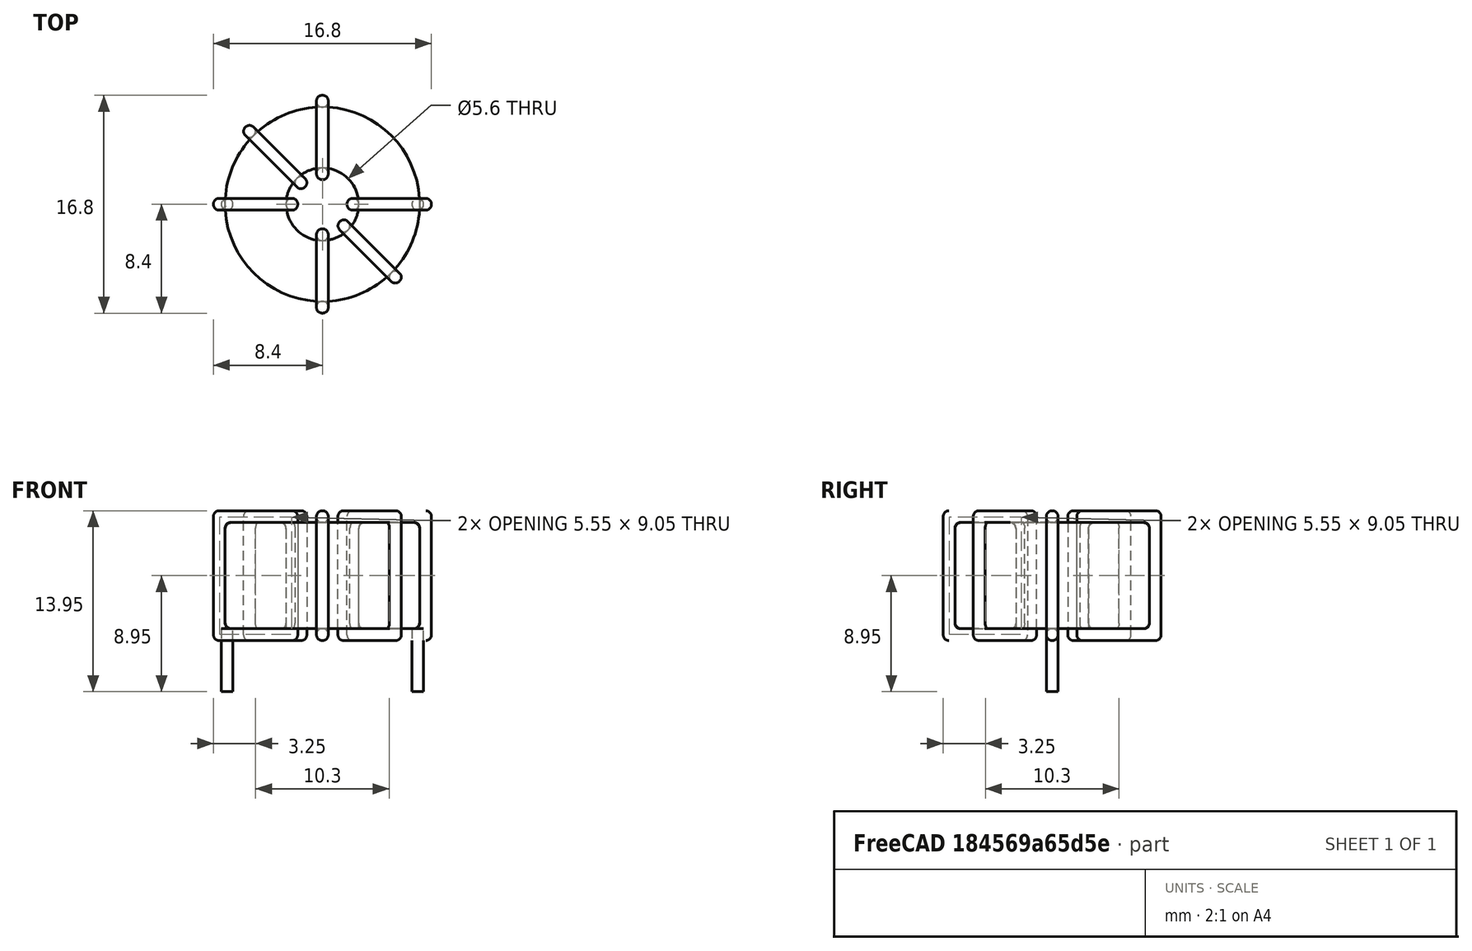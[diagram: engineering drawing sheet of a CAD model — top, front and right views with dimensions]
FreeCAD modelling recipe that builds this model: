
FCSTD DOCUMENT  (FreeCAD 0.16R6703 (Git))
Label: L_Toroid_Horizontal_D16.8mm_P14.70mm_Vishay_TJ3
License: All rights reserved
LicenseURL: http://en.wikipedia.org/wiki/All_rights_reserved
objects: Sketcher::SketchObject×6, PartDesign::Pad×6, PartDesign::Fillet×5, Spreadsheet::Sheet×1
note: 23 computed .brp shape members not serialized (recipe doc carries the construction recipe); baked Part::Feature solids carry a one-line shape summary decoded from their .brp

FEATURE [Spreadsheet::Sheet] Spreadsheet  label="dimensions"
  cells = A1=Wx; B1(Wx)=16.8; C1(WW)=5.600000000000001; D1=16.8; A2=Wy; B2(Wy)=16.8; D2=16.8; A3=RM; B3(RMx)=14.7; C3(RMy)=0; A4=d_wire; B4(d_wire)=0.8999999999999999; A5=H; B5(H)=8.199999999999999; A6=offsetx; B6(offsetx)=1.050000000000001
FEATURE [Sketcher::SketchObject] Sketch
  Placement = pos=(0,0,1.4) rot=(0,0,1;0rad)
  expr: Placement.Base.z = 0.5 + Spreadsheet.d_wire
  expr: Constraints[0] = Spreadsheet.Wx / 2 - Spreadsheet.d_wire
  expr: Constraints[4] = Spreadsheet.WW / 2
  expr: Constraints[2] = Spreadsheet.RMy / 2
  expr: Constraints[1] = Spreadsheet.RMx / 2
  sketch-geometry (2):
    g0: Circle CenterX=7.35 CenterY=0 CenterZ=0 NormalX=0 NormalY=0 NormalZ=1 Radius=7.5
    g1: Circle CenterX=7.35 CenterY=0 CenterZ=0 NormalX=0 NormalY=0 NormalZ=1 Radius=2.8
  constraints (5):
    c: Radius(g0) = 7.5
    c: DistanceX(g-1,g0) = 7.35
    c: DistanceY(g-1,g0) = 0
    c: Coincident(g1,g0)
    c: Radius(g1) = 2.8
FEATURE [PartDesign::Pad] Pad
  Length = 8.2
  Length2 = 100
  Placement = pos=(0,0,1.4) rot=(0,0,1;0rad)
  Sketch = -> Sketch
  Type = 0
  expr: Length = Spreadsheet.H
FEATURE [Sketcher::SketchObject] Sketch001
  Placement = pos=(0,0,0.95) rot=(0,0,1;0rad)
  expr: Placement.Base.z = 0.5 + Spreadsheet.d_wire * 0.5
  expr: Constraints[4] = Spreadsheet.RMx
  expr: Constraints[2] = Spreadsheet.RMy
  expr: Constraints[1] = Spreadsheet.d_wire / 2
  sketch-geometry (2):
    g0: Circle CenterX=0 CenterY=0 CenterZ=0 NormalX=0 NormalY=0 NormalZ=1 Radius=0.45
    g1: Circle CenterX=14.7 CenterY=0 CenterZ=0 NormalX=0 NormalY=0 NormalZ=1 Radius=0.45
  constraints (5):
    c: Equal(g0,g1)
    c: Radius(g0) = 0.45
    c: DistanceY(g-1,g1) = 0
    c: Coincident(g0,g-1)
    c: DistanceX(g-1,g1) = 14.7
FEATURE [PartDesign::Pad] Pad001
  Length = 0.45
  Length2 = 4.4
  Placement = pos=(0,0,0.95) rot=(0,0,1;0rad)
  Reversed = true
  Sketch = -> Sketch001
  Type = 4
  expr: Length2 = 3.5 + Spreadsheet.d_wire
  expr: Length = Spreadsheet.d_wire / 2
FEATURE [PartDesign::Fillet] Fillet
  Base = -> Pad [Edge6,Edge3,Edge2]
  Placement = pos=(0,0,1.4) rot=(0,0,1;0rad)
  Radius = 0.5
FEATURE [Sketcher::SketchObject] Sketch003
  Placement = pos=(7.35,0,0) rot=(1,0,0;1.5708rad)
  expr: Placement.Base.x = Spreadsheet.RMx / 2
  expr: Constraints[49] = Spreadsheet.Wx - Spreadsheet.d_wire * 2
  expr: Constraints[44] = Spreadsheet.d_wire
  expr: Constraints[23] = Spreadsheet.H
  expr: Constraints[22] = Spreadsheet.Wx / 2 - Spreadsheet.d_wire
  expr: Placement.Base.y = Spreadsheet.RMy / 2
  expr: Constraints[21] = (Spreadsheet.Wx - Spreadsheet.WW) / 2 - Spreadsheet.d_wire
  expr: Constraints[19] = Spreadsheet.d_wire
  expr: Constraints[17] = Spreadsheet.d_wire
  expr: Constraints[18] = Spreadsheet.d_wire
  expr: Constraints[16] = Spreadsheet.d_wire
  sketch-geometry (16):
    g0: LineSegment StartX=-1.9 StartY=0.5 StartZ=0 EndX=-8.4 EndY=0.5 EndZ=0
    g1: LineSegment StartX=-8.4 StartY=0.5 StartZ=0 EndX=-8.4 EndY=10.5 EndZ=0
    g2: LineSegment StartX=-8.4 StartY=10.5 StartZ=0 EndX=-1.9 EndY=10.5 EndZ=0
    g3: LineSegment StartX=-1.9 StartY=10.5 StartZ=0 EndX=-1.9 EndY=0.5 EndZ=0
    g4: LineSegment StartX=-7.5 StartY=9.6 StartZ=0 EndX=-2.8 EndY=9.6 EndZ=0
    g5: LineSegment StartX=-2.8 StartY=9.6 StartZ=0 EndX=-2.8 EndY=1.4 EndZ=0
    g6: LineSegment StartX=-2.8 StartY=1.4 StartZ=0 EndX=-7.5 EndY=1.4 EndZ=0
    g7: LineSegment StartX=-7.5 StartY=1.4 StartZ=0 EndX=-7.5 EndY=9.6 EndZ=0
    g8: LineSegment StartX=1.9 StartY=10.5 StartZ=0 EndX=8.4 EndY=10.5 EndZ=0
    g9: LineSegment StartX=8.4 StartY=10.5 StartZ=0 EndX=8.4 EndY=0.5 EndZ=0
    g10: LineSegment StartX=8.4 StartY=0.5 StartZ=0 EndX=1.9 EndY=0.5 EndZ=0
    g11: LineSegment StartX=1.9 StartY=0.5 StartZ=0 EndX=1.9 EndY=10.5 EndZ=0
    g12: LineSegment StartX=2.8 StartY=9.6 StartZ=0 EndX=7.5 EndY=9.6 EndZ=0
    g13: LineSegment StartX=7.5 StartY=9.6 StartZ=0 EndX=7.5 EndY=1.4 EndZ=0
    g14: LineSegment StartX=7.5 StartY=1.4 StartZ=0 EndX=2.8 EndY=1.4 EndZ=0
    g15: LineSegment StartX=2.8 StartY=1.4 StartZ=0 EndX=2.8 EndY=9.6 EndZ=0
  constraints (50):
    c: Horizontal(g0)
    c: Coincident(g1,g0)
    c: Vertical(g1)
    c: Coincident(g2,g1)
    c: Horizontal(g2)
    c: Coincident(g3,g2)
    c: Coincident(g3,g0)
    c: Vertical(g3)
    c: Coincident(g4,g5)
    c: Coincident(g5,g6)
    c: Coincident(g6,g7)
    c: Coincident(g7,g4)
    c: Horizontal(g4)
    c: Horizontal(g6)
    c: Vertical(g5)
    c: Vertical(g7)
    c: DistanceX(g1,g4) = 0.9
    c: DistanceY(g4,g1) = 0.9
    c: DistanceX(g5,g0) = 0.9
    c: DistanceY(g0,g5) = 0.9
    c: DistanceY(g-1,g0) = 0.5
    c: DistanceX(g6,g6) = 4.7
    c: DistanceX(g6,g-1) = 7.5
    c: DistanceY(g7,g7) = 8.2
    c: Coincident(g8,g9)
    c: Coincident(g9,g10)
    c: Coincident(g10,g11)
    c: Coincident(g11,g8)
    c: Horizontal(g8)
    c: Horizontal(g10)
    c: Vertical(g9)
    c: Vertical(g11)
    c: Coincident(g12,g13)
    c: Coincident(g13,g14)
    c: Coincident(g14,g15)
    c: Coincident(g15,g12)
    c: Horizontal(g12)
    c: Horizontal(g14)
    c: Vertical(g13)
    c: Vertical(g15)
    c: DistanceY(g8,g2) = 0
    c: DistanceY(g10,g0) = 0
    c: DistanceY(g14,g5) = 0
    c: DistanceY(g12,g4) = 0
    c: DistanceX(g8,g12) = 0.9
    c: Equal(g8,g2)
    c: Equal(g12,g4)
    c: Equal(g9,g1)
    c: Equal(g13,g7)
    c: DistanceX(g4,g12) = 15
FEATURE [PartDesign::Pad] Pad002
  Length = 0.9
  Length2 = 100
  Midplane = true
  Placement = pos=(7.35,0,0) rot=(1,0,0;1.5708rad)
  Sketch = -> Sketch003
  Type = 0
  expr: Length = Spreadsheet.d_wire
FEATURE [PartDesign::Fillet] Fillet001
  Base = -> Pad002 [Edge38,Edge41,Edge42,Edge43,Edge29,Edge32,Edge33,Edge34,Edge25,Edge35,Edge36,Edge13,Edge14,Edge15,Edge16,Edge17,Edge18,Edge19,Edge1,Edge2,Edge3,Edge4,Edge5,Edge6,Edge7,Edge37,Edge39,Edge40,Edge20,Edge23,Edge24,Edge21,Edge22,Edge8,Edge9,Edge10,Edge11,Edge12,Edge26,Edge27,+8 more]
  Placement = pos=(7.35,0,0) rot=(1,0,0;1.5708rad)
  Radius = 0.423
  expr: Radius = Spreadsheet.d_wire * 0.47
FEATURE [Sketcher::SketchObject] Sketch004
  Placement = pos=(7.35,0,0) rot=(0.862856,0.357407,0.357407;1.71777rad)
  expr: Placement.Base.x = Spreadsheet.RMx / 2
  expr: Constraints[49] = Spreadsheet.Wx - 2 * Spreadsheet.d_wire
  expr: Constraints[44] = Spreadsheet.d_wire
  expr: Constraints[23] = Spreadsheet.H
  expr: Constraints[22] = Spreadsheet.Wx / 2 - Spreadsheet.d_wire
  expr: Placement.Base.y = Spreadsheet.RMy / 2
  expr: Constraints[21] = (Spreadsheet.Wx - Spreadsheet.WW) / 2 - Spreadsheet.d_wire
  expr: Constraints[19] = Spreadsheet.d_wire
  expr: Constraints[17] = Spreadsheet.d_wire
  expr: Constraints[18] = Spreadsheet.d_wire
  expr: Constraints[16] = Spreadsheet.d_wire
  sketch-geometry (16):
    g0: LineSegment StartX=-1.9 StartY=0.5 StartZ=0 EndX=-8.4 EndY=0.5 EndZ=0
    g1: LineSegment StartX=-8.4 StartY=0.5 StartZ=0 EndX=-8.4 EndY=10.5 EndZ=0
    g2: LineSegment StartX=-8.4 StartY=10.5 StartZ=0 EndX=-1.9 EndY=10.5 EndZ=0
    g3: LineSegment StartX=-1.9 StartY=10.5 StartZ=0 EndX=-1.9 EndY=0.5 EndZ=0
    g4: LineSegment StartX=-7.5 StartY=9.6 StartZ=0 EndX=-2.8 EndY=9.6 EndZ=0
    g5: LineSegment StartX=-2.8 StartY=9.6 StartZ=0 EndX=-2.8 EndY=1.4 EndZ=0
    g6: LineSegment StartX=-2.8 StartY=1.4 StartZ=0 EndX=-7.5 EndY=1.4 EndZ=0
    g7: LineSegment StartX=-7.5 StartY=1.4 StartZ=0 EndX=-7.5 EndY=9.6 EndZ=0
    g8: LineSegment StartX=1.9 StartY=10.5 StartZ=0 EndX=8.4 EndY=10.5 EndZ=0
    g9: LineSegment StartX=8.4 StartY=10.5 StartZ=0 EndX=8.4 EndY=0.5 EndZ=0
    g10: LineSegment StartX=8.4 StartY=0.5 StartZ=0 EndX=1.9 EndY=0.5 EndZ=0
    g11: LineSegment StartX=1.9 StartY=0.5 StartZ=0 EndX=1.9 EndY=10.5 EndZ=0
    g12: LineSegment StartX=2.8 StartY=9.6 StartZ=0 EndX=7.5 EndY=9.6 EndZ=0
    g13: LineSegment StartX=7.5 StartY=9.6 StartZ=0 EndX=7.5 EndY=1.4 EndZ=0
    g14: LineSegment StartX=7.5 StartY=1.4 StartZ=0 EndX=2.8 EndY=1.4 EndZ=0
    g15: LineSegment StartX=2.8 StartY=1.4 StartZ=0 EndX=2.8 EndY=9.6 EndZ=0
  constraints (50):
    c: Horizontal(g0)
    c: Coincident(g1,g0)
    c: Vertical(g1)
    c: Coincident(g2,g1)
    c: Horizontal(g2)
    c: Coincident(g3,g2)
    c: Coincident(g3,g0)
    c: Vertical(g3)
    c: Coincident(g4,g5)
    c: Coincident(g5,g6)
    c: Coincident(g6,g7)
    c: Coincident(g7,g4)
    c: Horizontal(g4)
    c: Horizontal(g6)
    c: Vertical(g5)
    c: Vertical(g7)
    c: DistanceX(g1,g4) = 0.9
    c: DistanceY(g4,g1) = 0.9
    c: DistanceX(g5,g0) = 0.9
    c: DistanceY(g0,g5) = 0.9
    c: DistanceY(g-1,g0) = 0.5
    c: DistanceX(g6,g6) = 4.7
    c: DistanceX(g6,g-1) = 7.5
    c: DistanceY(g7,g7) = 8.2
    c: Coincident(g8,g9)
    c: Coincident(g9,g10)
    c: Coincident(g10,g11)
    c: Coincident(g11,g8)
    c: Horizontal(g8)
    c: Horizontal(g10)
    c: Vertical(g9)
    c: Vertical(g11)
    c: Coincident(g12,g13)
    c: Coincident(g13,g14)
    c: Coincident(g14,g15)
    c: Coincident(g15,g12)
    c: Horizontal(g12)
    c: Horizontal(g14)
    c: Vertical(g13)
    c: Vertical(g15)
    c: DistanceY(g8,g2) = 0
    c: DistanceY(g10,g0) = 0
    c: DistanceY(g14,g5) = 0
    c: DistanceY(g12,g4) = 0
    c: DistanceX(g8,g12) = 0.9
    c: Equal(g8,g2)
    c: Equal(g12,g4)
    c: Equal(g9,g1)
    c: Equal(g13,g7)
    c: DistanceX(g4,g12) = 15
FEATURE [PartDesign::Pad] Pad003
  Length = 0.9
  Length2 = 100
  Midplane = true
  Placement = pos=(7.35,0,0) rot=(0.862856,0.357407,0.357407;1.71777rad)
  Sketch = -> Sketch004
  Type = 0
  expr: Length = Spreadsheet.d_wire
FEATURE [PartDesign::Fillet] Fillet002
  Base = -> Pad003 [Edge38,Edge41,Edge42,Edge43,Edge29,Edge32,Edge33,Edge34,Edge25,Edge35,Edge36,Edge13,Edge14,Edge15,Edge16,Edge17,Edge18,Edge19,Edge1,Edge2,Edge3,Edge4,Edge5,Edge6,Edge7,Edge37,Edge39,Edge40,Edge20,Edge23,Edge24,Edge21,Edge22,Edge8,Edge9,Edge10,Edge11,Edge12,Edge26,Edge27,+8 more]
  Placement = pos=(7.35,0,0) rot=(0.862856,0.357407,0.357407;1.71777rad)
  Radius = 0.423
  expr: Radius = Spreadsheet.d_wire * 0.47
FEATURE [Sketcher::SketchObject] Sketch005
  Placement = pos=(7.35,0,0) rot=(0.862856,-0.357407,-0.357407;1.71777rad)
  expr: Placement.Base.x = Spreadsheet.RMx / 2
  expr: Constraints[49] = Spreadsheet.Wx - 2 * Spreadsheet.d_wire
  expr: Constraints[44] = Spreadsheet.d_wire
  expr: Constraints[23] = Spreadsheet.H
  expr: Constraints[22] = Spreadsheet.Wx / 2 - Spreadsheet.d_wire
  expr: Placement.Base.y = Spreadsheet.RMy / 2
  expr: Constraints[21] = (Spreadsheet.Wx - Spreadsheet.WW) / 2 - Spreadsheet.d_wire
  expr: Constraints[19] = Spreadsheet.d_wire
  expr: Constraints[17] = Spreadsheet.d_wire
  expr: Constraints[18] = Spreadsheet.d_wire
  expr: Constraints[16] = Spreadsheet.d_wire
  sketch-geometry (16):
    g0: LineSegment StartX=-1.9 StartY=0.5 StartZ=0 EndX=-8.4 EndY=0.5 EndZ=0
    g1: LineSegment StartX=-8.4 StartY=0.5 StartZ=0 EndX=-8.4 EndY=10.5 EndZ=0
    g2: LineSegment StartX=-8.4 StartY=10.5 StartZ=0 EndX=-1.9 EndY=10.5 EndZ=0
    g3: LineSegment StartX=-1.9 StartY=10.5 StartZ=0 EndX=-1.9 EndY=0.5 EndZ=0
    g4: LineSegment StartX=-7.5 StartY=9.6 StartZ=0 EndX=-2.8 EndY=9.6 EndZ=0
    g5: LineSegment StartX=-2.8 StartY=9.6 StartZ=0 EndX=-2.8 EndY=1.4 EndZ=0
    g6: LineSegment StartX=-2.8 StartY=1.4 StartZ=0 EndX=-7.5 EndY=1.4 EndZ=0
    g7: LineSegment StartX=-7.5 StartY=1.4 StartZ=0 EndX=-7.5 EndY=9.6 EndZ=0
    g8: LineSegment StartX=1.9 StartY=10.5 StartZ=0 EndX=8.4 EndY=10.5 EndZ=0
    g9: LineSegment StartX=8.4 StartY=10.5 StartZ=0 EndX=8.4 EndY=0.5 EndZ=0
    g10: LineSegment StartX=8.4 StartY=0.5 StartZ=0 EndX=1.9 EndY=0.5 EndZ=0
    g11: LineSegment StartX=1.9 StartY=0.5 StartZ=0 EndX=1.9 EndY=10.5 EndZ=0
    g12: LineSegment StartX=2.8 StartY=9.6 StartZ=0 EndX=7.5 EndY=9.6 EndZ=0
    g13: LineSegment StartX=7.5 StartY=9.6 StartZ=0 EndX=7.5 EndY=1.4 EndZ=0
    g14: LineSegment StartX=7.5 StartY=1.4 StartZ=0 EndX=2.8 EndY=1.4 EndZ=0
    g15: LineSegment StartX=2.8 StartY=1.4 StartZ=0 EndX=2.8 EndY=9.6 EndZ=0
  constraints (50):
    c: Horizontal(g0)
    c: Coincident(g1,g0)
    c: Vertical(g1)
    c: Coincident(g2,g1)
    c: Horizontal(g2)
    c: Coincident(g3,g2)
    c: Coincident(g3,g0)
    c: Vertical(g3)
    c: Coincident(g4,g5)
    c: Coincident(g5,g6)
    c: Coincident(g6,g7)
    c: Coincident(g7,g4)
    c: Horizontal(g4)
    c: Horizontal(g6)
    c: Vertical(g5)
    c: Vertical(g7)
    c: DistanceX(g1,g4) = 0.9
    c: DistanceY(g4,g1) = 0.9
    c: DistanceX(g5,g0) = 0.9
    c: DistanceY(g0,g5) = 0.9
    c: DistanceY(g-1,g0) = 0.5
    c: DistanceX(g6,g6) = 4.7
    c: DistanceX(g6,g-1) = 7.5
    c: DistanceY(g7,g7) = 8.2
    c: Coincident(g8,g9)
    c: Coincident(g9,g10)
    c: Coincident(g10,g11)
    c: Coincident(g11,g8)
    c: Horizontal(g8)
    c: Horizontal(g10)
    c: Vertical(g9)
    c: Vertical(g11)
    c: Coincident(g12,g13)
    c: Coincident(g13,g14)
    c: Coincident(g14,g15)
    c: Coincident(g15,g12)
    c: Horizontal(g12)
    c: Horizontal(g14)
    c: Vertical(g13)
    c: Vertical(g15)
    c: DistanceY(g8,g2) = 0
    c: DistanceY(g10,g0) = 0
    c: DistanceY(g14,g5) = 0
    c: DistanceY(g12,g4) = 0
    c: DistanceX(g8,g12) = 0.9
    c: Equal(g8,g2)
    c: Equal(g12,g4)
    c: Equal(g9,g1)
    c: Equal(g13,g7)
    c: DistanceX(g4,g12) = 15
FEATURE [PartDesign::Pad] Pad004
  Length = 0.9
  Length2 = 100
  Midplane = true
  Placement = pos=(7.35,0,0) rot=(0.862856,-0.357407,-0.357407;1.71777rad)
  Sketch = -> Sketch005
  Type = 0
  expr: Length = Spreadsheet.d_wire
FEATURE [PartDesign::Fillet] Fillet003
  Base = -> Pad004 [Edge38,Edge41,Edge42,Edge43,Edge29,Edge32,Edge33,Edge34,Edge25,Edge35,Edge36,Edge13,Edge14,Edge15,Edge16,Edge17,Edge18,Edge19,Edge1,Edge2,Edge3,Edge4,Edge5,Edge6,Edge7,Edge37,Edge39,Edge40,Edge20,Edge23,Edge24,Edge21,Edge22,Edge8,Edge9,Edge10,Edge11,Edge12,Edge26,Edge27,+8 more]
  Placement = pos=(7.35,0,0) rot=(0.862856,-0.357407,-0.357407;1.71777rad)
  Radius = 0.423
  expr: Radius = Spreadsheet.d_wire * 0.47
FEATURE [Sketcher::SketchObject] Sketch006
  Placement = pos=(7.35,0,0) rot=(0.57735,0.57735,0.57735;2.0944rad)
  expr: Placement.Base.x = Spreadsheet.RMx / 2
  expr: Constraints[49] = Spreadsheet.Wx - Spreadsheet.d_wire * 2
  expr: Constraints[44] = Spreadsheet.d_wire
  expr: Constraints[23] = Spreadsheet.H
  expr: Constraints[22] = Spreadsheet.Wx / 2 - Spreadsheet.d_wire
  expr: Placement.Base.y = Spreadsheet.RMy / 2
  expr: Constraints[21] = (Spreadsheet.Wx - Spreadsheet.WW) / 2 - Spreadsheet.d_wire
  expr: Constraints[19] = Spreadsheet.d_wire
  expr: Constraints[17] = Spreadsheet.d_wire
  expr: Constraints[18] = Spreadsheet.d_wire
  expr: Constraints[16] = Spreadsheet.d_wire
  sketch-geometry (16):
    g0: LineSegment StartX=-1.9 StartY=0.5 StartZ=0 EndX=-8.4 EndY=0.5 EndZ=0
    g1: LineSegment StartX=-8.4 StartY=0.5 StartZ=0 EndX=-8.4 EndY=10.5 EndZ=0
    g2: LineSegment StartX=-8.4 StartY=10.5 StartZ=0 EndX=-1.9 EndY=10.5 EndZ=0
    g3: LineSegment StartX=-1.9 StartY=10.5 StartZ=0 EndX=-1.9 EndY=0.5 EndZ=0
    g4: LineSegment StartX=-7.5 StartY=9.6 StartZ=0 EndX=-2.8 EndY=9.6 EndZ=0
    g5: LineSegment StartX=-2.8 StartY=9.6 StartZ=0 EndX=-2.8 EndY=1.4 EndZ=0
    g6: LineSegment StartX=-2.8 StartY=1.4 StartZ=0 EndX=-7.5 EndY=1.4 EndZ=0
    g7: LineSegment StartX=-7.5 StartY=1.4 StartZ=0 EndX=-7.5 EndY=9.6 EndZ=0
    g8: LineSegment StartX=1.9 StartY=10.5 StartZ=0 EndX=8.4 EndY=10.5 EndZ=0
    g9: LineSegment StartX=8.4 StartY=10.5 StartZ=0 EndX=8.4 EndY=0.5 EndZ=0
    g10: LineSegment StartX=8.4 StartY=0.5 StartZ=0 EndX=1.9 EndY=0.5 EndZ=0
    g11: LineSegment StartX=1.9 StartY=0.5 StartZ=0 EndX=1.9 EndY=10.5 EndZ=0
    g12: LineSegment StartX=2.8 StartY=9.6 StartZ=0 EndX=7.5 EndY=9.6 EndZ=0
    g13: LineSegment StartX=7.5 StartY=9.6 StartZ=0 EndX=7.5 EndY=1.4 EndZ=0
    g14: LineSegment StartX=7.5 StartY=1.4 StartZ=0 EndX=2.8 EndY=1.4 EndZ=0
    g15: LineSegment StartX=2.8 StartY=1.4 StartZ=0 EndX=2.8 EndY=9.6 EndZ=0
  constraints (50):
    c: Horizontal(g0)
    c: Coincident(g1,g0)
    c: Vertical(g1)
    c: Coincident(g2,g1)
    c: Horizontal(g2)
    c: Coincident(g3,g2)
    c: Coincident(g3,g0)
    c: Vertical(g3)
    c: Coincident(g4,g5)
    c: Coincident(g5,g6)
    c: Coincident(g6,g7)
    c: Coincident(g7,g4)
    c: Horizontal(g4)
    c: Horizontal(g6)
    c: Vertical(g5)
    c: Vertical(g7)
    c: DistanceX(g1,g4) = 0.9
    c: DistanceY(g4,g1) = 0.9
    c: DistanceX(g5,g0) = 0.9
    c: DistanceY(g0,g5) = 0.9
    c: DistanceY(g-1,g0) = 0.5
    c: DistanceX(g6,g6) = 4.7
    c: DistanceX(g6,g-1) = 7.5
    c: DistanceY(g7,g7) = 8.2
    c: Coincident(g8,g9)
    c: Coincident(g9,g10)
    c: Coincident(g10,g11)
    c: Coincident(g11,g8)
    c: Horizontal(g8)
    c: Horizontal(g10)
    c: Vertical(g9)
    c: Vertical(g11)
    c: Coincident(g12,g13)
    c: Coincident(g13,g14)
    c: Coincident(g14,g15)
    c: Coincident(g15,g12)
    c: Horizontal(g12)
    c: Horizontal(g14)
    c: Vertical(g13)
    c: Vertical(g15)
    c: DistanceY(g8,g2) = 0
    c: DistanceY(g10,g0) = 0
    c: DistanceY(g14,g5) = 0
    c: DistanceY(g12,g4) = 0
    c: DistanceX(g8,g12) = 0.9
    c: Equal(g8,g2)
    c: Equal(g12,g4)
    c: Equal(g9,g1)
    c: Equal(g13,g7)
    c: DistanceX(g4,g12) = 15
FEATURE [PartDesign::Pad] Pad005
  Length = 0.9
  Length2 = 100
  Midplane = true
  Placement = pos=(7.35,0,0) rot=(0.57735,0.57735,0.57735;2.0944rad)
  Sketch = -> Sketch006
  Type = 0
  expr: Length = Spreadsheet.d_wire
FEATURE [PartDesign::Fillet] Fillet004
  Base = -> Pad005 [Edge38,Edge41,Edge42,Edge43,Edge29,Edge32,Edge33,Edge34,Edge25,Edge35,Edge36,Edge13,Edge14,Edge15,Edge16,Edge17,Edge18,Edge19,Edge1,Edge2,Edge3,Edge4,Edge5,Edge6,Edge7,Edge37,Edge39,Edge40,Edge20,Edge23,Edge24,Edge21,Edge22,Edge8,Edge9,Edge10,Edge11,Edge12,Edge26,Edge27,+8 more]
  Placement = pos=(7.35,0,0) rot=(0.57735,0.57735,0.57735;2.0944rad)
  Radius = 0.423
  expr: Radius = Spreadsheet.d_wire * 0.47
